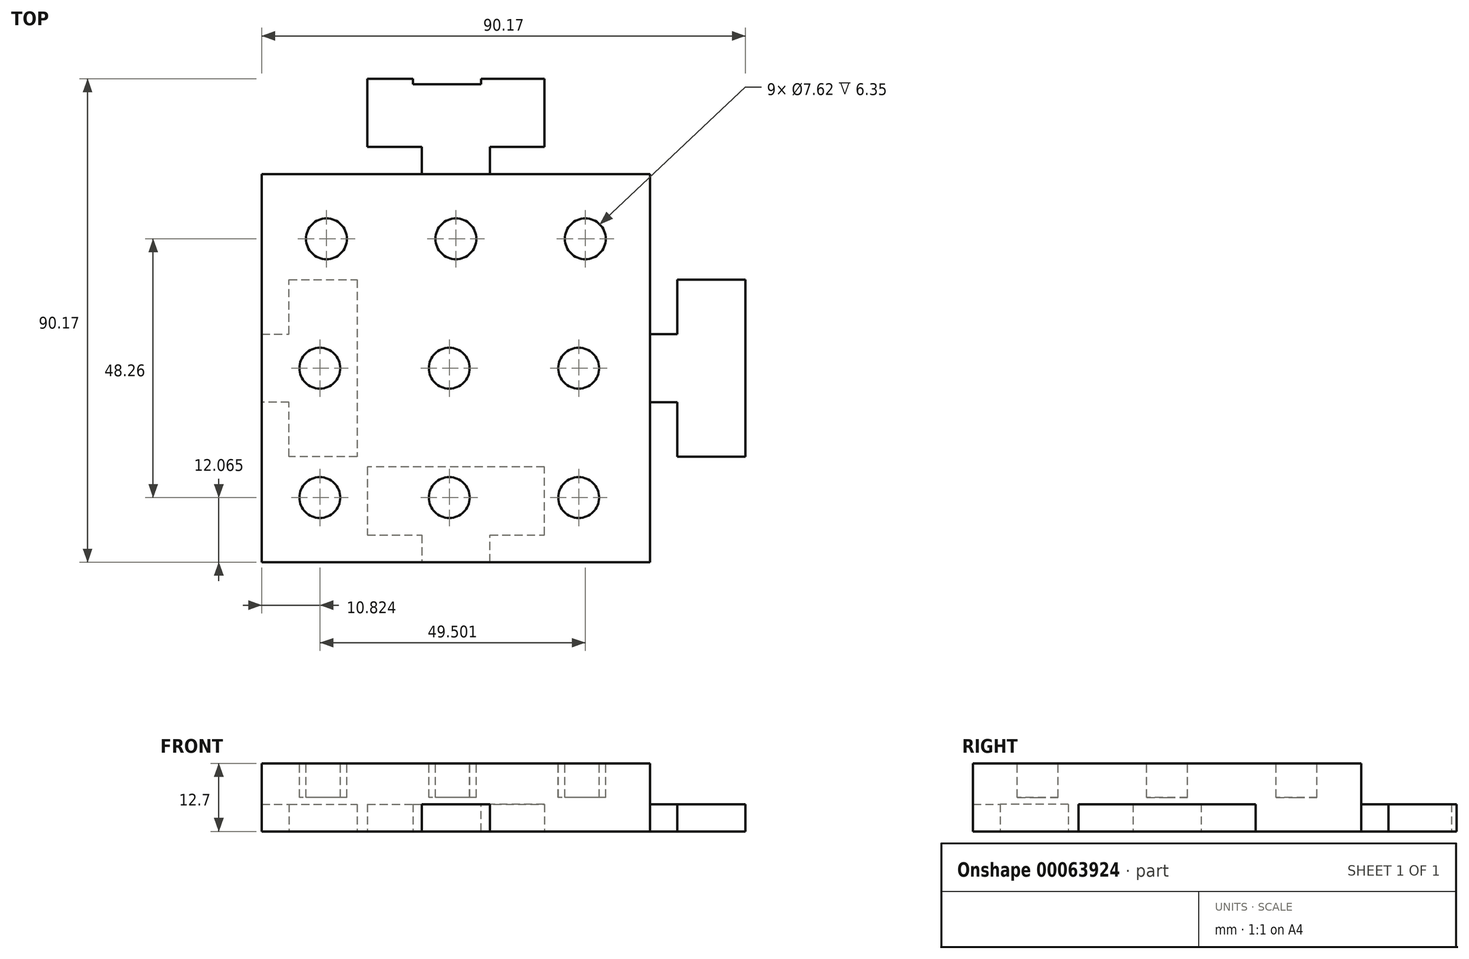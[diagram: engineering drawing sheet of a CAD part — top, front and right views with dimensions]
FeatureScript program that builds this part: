
annotation { "Feature Type Name" : "Feature", "Feature Type Description" : "" }
export const myFeature = defineFeature(function(context is Context, id is Id, definition is map)
    precondition{}
    {
        {
            var Q0;
            Q0=qCreatedBy(makeId("Top.planeOp"),FACE);
            var sketch = newSketch(context, id + "F0", { "sketchPlane" : qUnion([Q0])});
            skLineSegment(sketch, "E0.bottom", {"start": v(0, 0) * mm, "end": v(-72.4, 0) * mm});
            skLineSegment(sketch, "E0.top", {"start": v(0, -72.4) * mm, "end": v(-72.39, -72.4) * mm});
            skLineSegment(sketch, "E0.left", {"start": v(0, 0) * mm, "end": v(0, -72.4) * mm});
            skLineSegment(sketch, "E0.right", {"start": v(-72.4, 0) * mm, "end": v(-72.39, -72.4) * mm});
            skSolve(sketch);
        }
        {
            var Q0;
            Q0 = qSketchRegion(id + "F0", true);
            extrude(context, id + "F1", {"entities" : qUnion([Q0]), "depth" : 12.7 * mm});
        }
        {
            var Q0;
            Q0=makeQuery(id+"F1.opExtrude","CAP_FACE",FACE,{"disambiguationData":[OSD([sQuery(id+"F0.wireOp",EDGE,"E0.bottom"),sQuery(id+"F0.wireOp",EDGE,"E0.top"),sQuery(id+"F0.wireOp",EDGE,"E0.left"),sQuery(id+"F0.wireOp",EDGE,"E0.right")])],"isStart":false});
            var sketch = newSketch(context, id + "F2", { "sketchPlane" : qUnion([Q0])});
            skCircle(sketch, "E1", {"center": v(-60.33, -12.06) * mm, "radius": 3.81 * mm});
            skCircle(sketch, "E2", {"center": v(-61.57, -36.2) * mm, "radius": 3.81 * mm});
            skCircle(sketch, "E3", {"center": v(-61.56, -60.33) * mm, "radius": 3.81 * mm});
            skCircle(sketch, "E4", {"center": v(-36.2, -12.07) * mm, "radius": 3.81 * mm});
            skCircle(sketch, "E5", {"center": v(-37.44, -36.2) * mm, "radius": 3.81 * mm});
            skCircle(sketch, "E6", {"center": v(-37.43, -60.33) * mm, "radius": 3.81 * mm});
            skCircle(sketch, "E7", {"center": v(-12.07, -12.06) * mm, "radius": 3.81 * mm});
            skCircle(sketch, "E8", {"center": v(-13.3, -36.2) * mm, "radius": 3.81 * mm});
            skCircle(sketch, "E9", {"center": v(-13.3, -60.33) * mm, "radius": 3.81 * mm});
            skSolve(sketch);
        }
        {
            var Q0;
            Q0 = qSketchRegion(id + "F2", true);
            extrude(context, id + "F3", {"entities" : qUnion([Q0]), "operationType" : NewBodyOperationType.REMOVE, "oppositeDirection" : true, "depth" : 6.35 * mm});
        }
        {
            var Q0;
            Q0=makeQuery(id+"F1.opExtrude","CAP_FACE",FACE,{"disambiguationData":[OSD([sQuery(id+"F0.wireOp",EDGE,"E0.bottom"),sQuery(id+"F0.wireOp",EDGE,"E0.top"),sQuery(id+"F0.wireOp",EDGE,"E0.left"),sQuery(id+"F0.wireOp",EDGE,"E0.right")])],"isStart":true});
            var sketch = newSketch(context, id + "F4", { "sketchPlane" : qUnion([Q0])});
            skPoint(sketch, "E10.endSnap0", {"position": v(0, 36.2) * mm});
            skLineSegment(sketch, "E11", {"start": v(0, 42.55) * mm, "end": v(5.08, 42.55) * mm});
            skLineSegment(sketch, "E12", {"start": v(0, 29.85) * mm, "end": v(5.08, 29.85) * mm});
            skLineSegment(sketch, "E13", {"start": v(0, 42.55) * mm, "end": v(0, 29.85) * mm});
            skLineSegment(sketch, "E14", {"start": v(5.08, 42.55) * mm, "end": v(5.08, 52.7) * mm});
            skLineSegment(sketch, "E15", {"start": v(5.08, 29.85) * mm, "end": v(5.08, 19.69) * mm});
            skLineSegment(sketch, "E16", {"start": v(5.08, 52.7) * mm, "end": v(17.78, 52.7) * mm});
            skLineSegment(sketch, "E17", {"start": v(17.78, 52.7) * mm, "end": v(17.78, 19.69) * mm});
            skLineSegment(sketch, "E18", {"start": v(17.78, 19.69) * mm, "end": v(5.08, 19.69) * mm});
            skLineSegment(sketch, "E19", {"start": v(-29.85, 0) * mm, "end": v(-42.55, 0) * mm});
            skLineSegment(sketch, "E20", {"start": v(-42.55, 0) * mm, "end": v(-42.55, -5.08) * mm});
            skLineSegment(sketch, "E21", {"start": v(-42.55, -5.08) * mm, "end": v(-52.7, -5.08) * mm});
            skLineSegment(sketch, "E22", {"start": v(-52.7, -5.08) * mm, "end": v(-52.7, -17.78) * mm});
            skLineSegment(sketch, "E23", {"start": v(-52.7, -17.78) * mm, "end": v(-19.69, -17.78) * mm});
            skLineSegment(sketch, "E24", {"start": v(-19.69, -17.78) * mm, "end": v(-19.69, -5.08) * mm});
            skLineSegment(sketch, "E25", {"start": v(-19.69, -5.08) * mm, "end": v(-29.85, -5.08) * mm});
            skLineSegment(sketch, "E26", {"start": v(-29.85, -5.08) * mm, "end": v(-29.85, 0) * mm});
            skSolve(sketch);
        }
        {
            var Q0;
            Q0 = qSketchRegion(id + "F4", true);
            extrude(context, id + "F5", {"entities" : qUnion([Q0]), "oppositeDirection" : true, "depth" : 5.08 * mm});
        }
        {
            var Q0;
            Q0=makeQuery(id+"F1.opExtrude","CAP_FACE",FACE,{"disambiguationData":[OSD([sQuery(id+"F0.wireOp",EDGE,"E0.bottom"),sQuery(id+"F0.wireOp",EDGE,"E0.top"),sQuery(id+"F0.wireOp",EDGE,"E0.left"),sQuery(id+"F0.wireOp",EDGE,"E0.right")])],"isStart":true});
            var sketch = newSketch(context, id + "F6", { "sketchPlane" : qUnion([Q0])});
            skPoint(sketch, "E27.endSnap0", {"position": v(-56.89, -35.83) * mm});
            skLineSegment(sketch, "E28", {"start": v(-56.89, -29.48) * mm, "end": v(-44.19, -29.48) * mm});
            skLineSegment(sketch, "E29", {"start": v(-56.89, -42.18) * mm, "end": v(-44.19, -42.18) * mm});
            skLineSegment(sketch, "E30", {"start": v(-56.89, -29.48) * mm, "end": v(-56.89, -42.18) * mm});
            skLineSegment(sketch, "E31", {"start": v(-44.19, -29.48) * mm, "end": v(-44.19, -16.78) * mm});
            skLineSegment(sketch, "E32", {"start": v(-44.19, -42.18) * mm, "end": v(-44.19, -54.88) * mm});
            skLineSegment(sketch, "E33", {"start": v(-44.19, -16.78) * mm, "end": v(-31.49, -16.78) * mm});
            skLineSegment(sketch, "E34", {"start": v(-31.49, -16.78) * mm, "end": v(-31.49, -54.88) * mm});
            skLineSegment(sketch, "E35", {"start": v(-31.49, -54.88) * mm, "end": v(-44.19, -54.88) * mm});
            skLineSegment(sketch, "E36", {"start": v(-42.54, 72.4) * mm, "end": v(-29.84, 72.4) * mm});
            skLineSegment(sketch, "E37", {"start": v(-29.84, 72.4) * mm, "end": v(-29.84, 67.31) * mm});
            skLineSegment(sketch, "E38", {"start": v(-29.84, 67.31) * mm, "end": v(-19.68, 67.31) * mm});
            skLineSegment(sketch, "E39", {"start": v(-19.68, 67.31) * mm, "end": v(-19.68, 54.61) * mm});
            skLineSegment(sketch, "E40", {"start": v(-19.68, 54.61) * mm, "end": v(-52.7, 54.6) * mm});
            skLineSegment(sketch, "E41", {"start": v(-52.7, 54.6) * mm, "end": v(-52.7, 67.3) * mm});
            skLineSegment(sketch, "E42", {"start": v(-52.7, 67.3) * mm, "end": v(-42.54, 67.3) * mm});
            skLineSegment(sketch, "E43", {"start": v(-42.54, 67.3) * mm, "end": v(-42.54, 72.4) * mm});
            skLineSegment(sketch, "E44", {"start": v(-42.55, 0) * mm, "end": v(-29.85, 0) * mm});
            skLineSegment(sketch, "E45", {"start": v(-72.39, 42.55) * mm, "end": v(-72.39, 29.85) * mm});
            skLineSegment(sketch, "E46", {"start": v(-72.39, 29.85) * mm, "end": v(-67.3, 29.85) * mm});
            skLineSegment(sketch, "E47", {"start": v(-67.3, 29.84) * mm, "end": v(-67.3, 19.69) * mm});
            skLineSegment(sketch, "E48", {"start": v(-67.3, 19.69) * mm, "end": v(-54.6, 19.69) * mm});
            skLineSegment(sketch, "E49", {"start": v(-54.6, 19.69) * mm, "end": v(-54.6, 52.7) * mm});
            skLineSegment(sketch, "E50", {"start": v(-54.6, 52.7) * mm, "end": v(-67.3, 52.7) * mm});
            skLineSegment(sketch, "E51", {"start": v(-67.3, 52.7) * mm, "end": v(-67.3, 42.55) * mm});
            skLineSegment(sketch, "E52", {"start": v(-67.3, 42.55) * mm, "end": v(-72.39, 42.55) * mm});
            skSolve(sketch);
        }
        {
            var Q0;
            Q0 = qSketchRegion(id + "F6", true);
            extrude(context, id + "F7", {"entities" : qUnion([Q0]), "operationType" : NewBodyOperationType.REMOVE, "oppositeDirection" : true, "depth" : 5.08 * mm});
        }
        {
            var Q0;
            Q0=makeQuery(id+"F1.opExtrude","CAP_FACE",FACE,{"disambiguationData":[OSD([sQuery(id+"F0.wireOp",EDGE,"E0.bottom"),sQuery(id+"F0.wireOp",EDGE,"E0.top"),sQuery(id+"F0.wireOp",EDGE,"E0.left"),sQuery(id+"F0.wireOp",EDGE,"E0.right")])],"isStart":true});
            var sketch = newSketch(context, id + "F8", { "sketchPlane" : qUnion([Q0])});
            skLineSegment(sketch, "E53.bottom", {"start": v(-34.41, -3.75) * mm, "end": v(-38.54, -3.75) * mm});
            skLineSegment(sketch, "E53.top", {"start": v(-34.41, 3.3) * mm, "end": v(-38.54, 3.3) * mm});
            skLineSegment(sketch, "E53.left", {"start": v(-34.41, -3.75) * mm, "end": v(-34.41, 3.3) * mm});
            skLineSegment(sketch, "E53.right", {"start": v(-38.54, -3.75) * mm, "end": v(-38.54, 3.3) * mm});
            skLineSegment(sketch, "E54.bottom", {"start": v(4.18, 32.27) * mm, "end": v(-10.19, 32.27) * mm});
            skLineSegment(sketch, "E54.top", {"start": v(4.18, 37.93) * mm, "end": v(-10.19, 37.93) * mm});
            skLineSegment(sketch, "E54.left", {"start": v(4.18, 32.27) * mm, "end": v(4.18, 37.93) * mm});
            skLineSegment(sketch, "E54.right", {"start": v(-10.19, 32.27) * mm, "end": v(-10.19, 37.93) * mm});
            skSolve(sketch);
        }
        {
            var Q0;
            Q0 = qSketchRegion(id + "F8", true);
            extrude(context, id + "F9", {"entities" : qUnion([Q0]), "operationType" : NewBodyOperationType.ADD, "oppositeDirection" : true, "depth" : 2.54 * mm});
        }
    });
